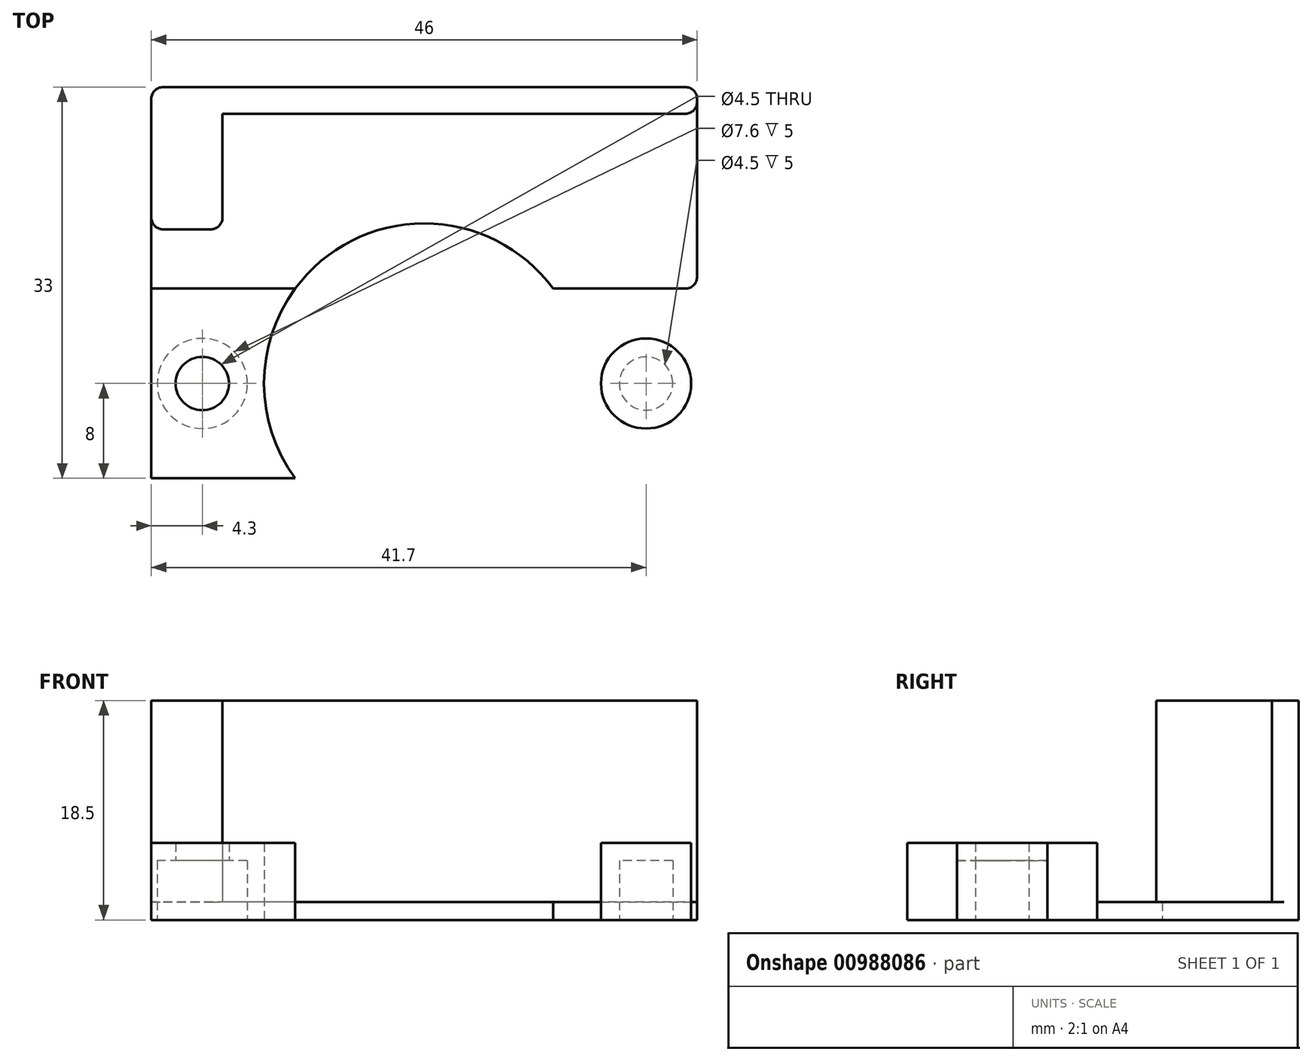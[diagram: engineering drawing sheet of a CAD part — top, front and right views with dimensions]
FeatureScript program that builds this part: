
annotation { "Feature Type Name" : "Feature", "Feature Type Description" : "" }
export const myFeature = defineFeature(function(context is Context, id is Id, definition is map)
    precondition{}
    {
        {
            var Q0;
            Q0=qCreatedBy(makeId("Top.planeOp"),FACE);
            var sketch = newSketch(context, id + "F0", { "sketchPlane" : qUnion([Q0])});
            skLineSegment(sketch, "E0.bottom", {"start": v(-23, 16.5) * mm, "end": v(23, 16.5) * mm});
            skLineSegment(sketch, "E0.top", {"start": v(-23, -16.5) * mm, "end": v(23, -16.5) * mm});
            skLineSegment(sketch, "E0.left", {"start": v(-23, 16.5) * mm, "end": v(-23, -16.5) * mm});
            skLineSegment(sketch, "E0.right", {"start": v(23, 16.5) * mm, "end": v(23, -16.5) * mm});
            skPoint(sketch, "E0.middle", {"position": v(0, 0) * mm});
            skPoint(sketch, "E1", {"position": v(0, -16.5) * mm});
            skCircle(sketch, "E2", {"center": v(-18.7, -8.5) * mm, "radius": 2.25 * mm});
            skLineSegment(sketch, "E3", {"start": v(0, 16.5) * mm, "end": v(0, -16.5) * mm, "construction": true});
            skCircle(sketch, "E4.MirrorC", {"center": v(18.7, -8.5) * mm, "radius": 2.25 * mm});
            skLineSegment(sketch, "E5", {"start": v(18.7, -8.5) * mm, "end": v(-18.7, -8.5) * mm, "construction": true});
            skCircle(sketch, "E6", {"center": v(0, -8.5) * mm, "radius": 13.5 * mm});
            skCircle(sketch, "E7", {"center": v(-18.7, -8.5) * mm, "radius": 3.8 * mm});
            skCircle(sketch, "E8.MirrorC", {"center": v(18.7, -8.5) * mm, "radius": 3.8 * mm});
            skLineSegment(sketch, "E9.bottom", {"start": v(-23, -0.5) * mm, "end": v(23, -0.5) * mm});
            skLineSegment(sketch, "E9.left", {"start": v(-23, -0.5) * mm, "end": v(-23, -16.5) * mm});
            skLineSegment(sketch, "E9.right", {"start": v(23, -0.5) * mm, "end": v(23, -16.5) * mm});
            skSolve(sketch);
        }
        {
            var Q0;
            Q0=makeQuery(id+"F0.imprint","IMPRINT",FACE,{"disambiguationData":[TD([[makeQuery(id+"F0.imprint","IMPRINT",EDGE,{"derivedFrom":sQuery(id+"F0.wireOp",EDGE,"E7")}),-1.0]])]});
            var Q1;
            Q1=makeQuery(id+"F0.imprint","IMPRINT",FACE,{"disambiguationData":[TD([[makeQuery(id+"F0.imprint","IMPRINT",EDGE,{"derivedFrom":sQuery(id+"F0.wireOp",EDGE,"E0.bottom")}),-1.0]])]});
            var Q2;
            Q2=makeQuery(id+"F0.imprint","IMPRINT",FACE,{"disambiguationData":[TD([[makeQuery(id+"F0.imprint","IMPRINT",EDGE,{"derivedFrom":sQuery(id+"F0.wireOp",EDGE,"E8.MirrorC")}),1.0]])]});
            extrude(context, id + "F1", {"entities" : qUnion([Q0, Q1, Q2]), "depth" : 1.5 * mm, "offsetDistance" : 25 * mm});
        }
        {
            var Q0;
            Q0=makeQuery(id+"F1.opExtrude","CAP_FACE",FACE,{"disambiguationData":[OSD([sQuery(id+"F0.wireOp",EDGE,"E0.bottom"),sQuery(id+"F0.wireOp",EDGE,"E0.top"),sQuery(id+"F0.wireOp",EDGE,"E0.left"),sQuery(id+"F0.wireOp",EDGE,"E0.right"),sQuery(id+"F0.wireOp",EDGE,"xRUmQ0dG-i3N2-o9Ad-kzeh-Mr6nwe9xlCmq.top"),sQuery(id+"F0.wireOp",EDGE,"xRUmQ0dG-i3N2-o9Ad-kzeh-Mr6nwe9xlCmq.left"),sQuery(id+"F0.wireOp",EDGE,"xRUmQ0dG-i3N2-o9Ad-kzeh-Mr6nwe9xlCmq.right"),sQuery(id+"F0.wireOp",EDGE,"E2"),sQuery(id+"F0.wireOp",EDGE,"E4.MirrorC")])],"isStart":false});
            var sketch = newSketch(context, id + "F2", { "sketchPlane" : qUnion([Q0])});
            skLineSegment(sketch, "E10.bottom", {"start": v(-23, 16.5) * mm, "end": v(23, 16.5) * mm});
            skLineSegment(sketch, "E10.top", {"start": v(-23, 4.5) * mm, "end": v(23, 4.5) * mm});
            skLineSegment(sketch, "E10.left", {"start": v(-23, 16.5) * mm, "end": v(-23, 4.5) * mm});
            skLineSegment(sketch, "E10.right", {"start": v(23, 16.5) * mm, "end": v(23, 4.5) * mm});
            skLineSegment(sketch, "E11.bottom", {"start": v(23, 6.75) * mm, "end": v(-17, 6.75) * mm});
            skLineSegment(sketch, "E11.top", {"start": v(23, 14.25) * mm, "end": v(-17, 14.25) * mm});
            skLineSegment(sketch, "E11.left", {"start": v(23, 14.25) * mm, "end": v(23, 6.75) * mm});
            skLineSegment(sketch, "E11.right", {"start": v(-17, 14.25) * mm, "end": v(-17, 6.75) * mm});
            skPoint(sketch, "E12", {"position": v(23, 10.5) * mm});
            skLineSegment(sketch, "E13.bottom", {"start": v(14, 6.75) * mm, "end": v(23, 6.75) * mm});
            skLineSegment(sketch, "E13.top", {"start": v(14, 4.5) * mm, "end": v(23, 4.5) * mm});
            skLineSegment(sketch, "E13.left", {"start": v(14, 6.75) * mm, "end": v(14, 4.5) * mm});
            skLineSegment(sketch, "E13.right", {"start": v(23, 6.75) * mm, "end": v(23, 4.5) * mm});
            skLineSegment(sketch, "E14.bottom", {"start": v(-17, 6.75) * mm, "end": v(-12, 6.75) * mm});
            skLineSegment(sketch, "E14.left", {"start": v(-17, 6.75) * mm, "end": v(-17, 4.5) * mm});
            skLineSegment(sketch, "E15", {"start": v(-12, 6.75) * mm, "end": v(-12, 4.5) * mm});
            skSolve(sketch);
        }
        {
            var Q0;
            Q0=makeQuery(id+"F2.imprint","IMPRINT",FACE,{"disambiguationData":[TD([[makeQuery(id+"F2.imprint","IMPRINT",EDGE,{"derivedFrom":sQuery(id+"F2.wireOp",EDGE,"E10.bottom")}),-1.0]])]});
            var Q1;
            Q1=makeQuery(id+"F2.imprint","IMPRINT",FACE,{"disambiguationData":[TD([[makeQuery(id+"F2.imprint","IMPRINT",EDGE,{"derivedFrom":sQuery(id+"F2.wireOp",EDGE,"E14.bottom")}),-1.0]])]});
            var Q2;
            Q2=makeQuery(id+"F2.imprint","IMPRINT",FACE,{"disambiguationData":[TD([[makeQuery(id+"F2.imprint","IMPRINT",EDGE,{"derivedFrom":sQuery(id+"F2.wireOp",EDGE,"E13.bottom")}),-1.0]])]});
            extrude(context, id + "F3", {"entities" : qUnion([Q0, Q1, Q2]), "operationType" : NewBodyOperationType.ADD, "depth" : 17 * mm, "offsetDistance" : 25 * mm});
        }
        {
            var Q0;
            Q0=makeQuery(id+"F3.boolean.opBoolean","MERGE",EDGE,{"derivedFrom":[makeQuery(id+"F1.opExtrude","SWEPT_EDGE",EDGE,{"disambiguationData":[OSD([sQuery(id+"F0.wireOp",EDGE,"E0.bottom"),sQuery(id+"F0.wireOp",EDGE,"E0.left")])]}),makeQuery(id+"F3.opExtrude","SWEPT_EDGE",EDGE,{"disambiguationData":[OSD([sQuery(id+"F2.wireOp",EDGE,"E10.bottom"),sQuery(id+"F2.wireOp",EDGE,"E10.left")])]})]});
            var Q1;
            Q1=makeQuery(id+"F3.boolean.opBoolean","MERGE",EDGE,{"derivedFrom":[makeQuery(id+"F1.opExtrude","SWEPT_EDGE",EDGE,{"disambiguationData":[OSD([sQuery(id+"F0.wireOp",EDGE,"E0.bottom"),sQuery(id+"F0.wireOp",EDGE,"E0.right")])]}),makeQuery(id+"F3.opExtrude","SWEPT_EDGE",EDGE,{"disambiguationData":[OSD([sQuery(id+"F2.wireOp",EDGE,"E10.bottom"),sQuery(id+"F2.wireOp",EDGE,"E10.right")])]})]});
            var Q2;
            Q2=makeQuery(id+"F3.opExtrude","SWEPT_EDGE",EDGE,{"disambiguationData":[OSD([sQuery(id+"F2.wireOp",EDGE,"E10.right"),sQuery(id+"F2.wireOp",EDGE,"E11.top"),sQuery(id+"F2.wireOp",EDGE,"E11.left")])]});
            var Q3;
            Q3=makeQuery(id+"F3.opExtrude","SWEPT_EDGE",EDGE,{"disambiguationData":[OSD([sQuery(id+"F2.wireOp",EDGE,"E11.left"),sQuery(id+"F2.wireOp",EDGE,"E13.bottom"),sQuery(id+"F2.wireOp",EDGE,"E13.right")])]});
            var Q4;
            Q4=makeQuery(id+"F3.opExtrude","SWEPT_EDGE",EDGE,{"disambiguationData":[OSD([sQuery(id+"F0.wireOp",EDGE,"E0.right"),sQuery(id+"F2.wireOp",EDGE,"E13.top"),sQuery(id+"F2.wireOp",EDGE,"E13.right")])]});
            var Q5;
            Q5=makeQuery(id+"F3.opExtrude","SWEPT_EDGE",EDGE,{"disambiguationData":[OSD([sQuery(id+"F2.wireOp",EDGE,"E11.bottom"),sQuery(id+"F2.wireOp",EDGE,"E14.bottom"),sQuery(id+"F2.wireOp",EDGE,"E14.right")])]});
            var Q6;
            Q6=makeQuery(id+"F3.opExtrude","SWEPT_EDGE",EDGE,{"disambiguationData":[OSD([sQuery(id+"F2.wireOp",EDGE,"E10.top"),sQuery(id+"F2.wireOp",EDGE,"E14.top"),sQuery(id+"F2.wireOp",EDGE,"E14.right")])]});
            var Q7;
            Q7=makeQuery(id+"F1.opExtrude","SWEPT_EDGE",EDGE,{"disambiguationData":[OSD([sQuery(id+"F0.wireOp",EDGE,"E0.top"),sQuery(id+"F0.wireOp",EDGE,"xRUmQ0dG-i3N2-o9Ad-kzeh-Mr6nwe9xlCmq.bottom"),sQuery(id+"F0.wireOp",EDGE,"xRUmQ0dG-i3N2-o9Ad-kzeh-Mr6nwe9xlCmq.left")])]});
            var Q8;
            Q8=makeQuery(id+"F1.opExtrude","SWEPT_EDGE",EDGE,{"disambiguationData":[OSD([sQuery(id+"F0.wireOp",EDGE,"E0.top"),sQuery(id+"F0.wireOp",EDGE,"E0.right")])]});
            var Q9;
            Q9=makeQuery(id+"F1.opExtrude","SWEPT_EDGE",EDGE,{"disambiguationData":[OSD([sQuery(id+"F0.wireOp",EDGE,"E0.top"),sQuery(id+"F0.wireOp",EDGE,"xRUmQ0dG-i3N2-o9Ad-kzeh-Mr6nwe9xlCmq.bottom"),sQuery(id+"F0.wireOp",EDGE,"xRUmQ0dG-i3N2-o9Ad-kzeh-Mr6nwe9xlCmq.right")])]});
            var Q10;
            Q10=makeQuery(id+"F1.opExtrude","SWEPT_EDGE",EDGE,{"disambiguationData":[OSD([sQuery(id+"F0.wireOp",EDGE,"E0.top"),sQuery(id+"F0.wireOp",EDGE,"E0.left")])]});
            var Q11;
            Q11=makeQuery(id+"F3.opExtrude","SWEPT_EDGE",EDGE,{"disambiguationData":[OSD([sQuery(id+"F0.wireOp",EDGE,"E0.left"),sQuery(id+"F2.wireOp",EDGE,"E10.top"),sQuery(id+"F2.wireOp",EDGE,"E10.left")])]});
            var Q12;
            Q12=makeQuery(id+"F3.opExtrude","SWEPT_EDGE",EDGE,{"disambiguationData":[OSD([sQuery(id+"F2.wireOp",EDGE,"E10.top"),sQuery(id+"F2.wireOp",EDGE,"E13.top"),sQuery(id+"F2.wireOp",EDGE,"E13.left")])]});
            var Q13;
            Q13=makeQuery(id+"F3.opExtrude","SWEPT_EDGE",EDGE,{"disambiguationData":[OSD([sQuery(id+"F2.wireOp",EDGE,"E11.bottom"),sQuery(id+"F2.wireOp",EDGE,"E13.bottom"),sQuery(id+"F2.wireOp",EDGE,"E13.left")])]});
            fillet(context, id + "F4", {"entities" : qUnion([Q0, Q1, Q2, Q3, Q4, Q5, Q6, Q7, Q8, Q9, Q10, Q11, Q12, Q13]), "radius" : 1 * mm, "tangentPropagation" : true, "allowEdgeOverflow" : false});
        }
        {
            var Q0;
            Q0=makeQuery(id+"F0.imprint","IMPRINT",FACE,{"disambiguationData":[TD([[makeQuery(id+"F0.imprint","IMPRINT",EDGE,{"derivedFrom":sQuery(id+"F0.wireOp",EDGE,"E7")}),-1.0]])]});
            var Q1;
            Q1=makeQuery(id+"F0.imprint","IMPRINT",FACE,{"disambiguationData":[TD([[makeQuery(id+"F0.imprint","IMPRINT",EDGE,{"derivedFrom":sQuery(id+"F0.wireOp",EDGE,"E8.MirrorC")}),1.0]])]});
            var Q2;
            Q2=makeQuery(id+"F0.imprint","IMPRINT",FACE,{"disambiguationData":[TD([[makeQuery(id+"F0.imprint","IMPRINT",EDGE,{"derivedFrom":sQuery(id+"F0.wireOp",EDGE,"E2")}),-1.0]])]});
            var Q3;
            Q3=makeQuery(id+"F0.imprint","IMPRINT",FACE,{"disambiguationData":[TD([[makeQuery(id+"F0.imprint","IMPRINT",EDGE,{"derivedFrom":sQuery(id+"F0.wireOp",EDGE,"E4.MirrorC")}),1.0]])]});
            extrude(context, id + "F5", {"entities" : qUnion([Q0, Q1, Q2, Q3]), "operationType" : NewBodyOperationType.ADD, "depth" : 6.5 * mm, "offsetDistance" : 25 * mm});
        }
        {
            var Q0;
            Q0=makeQuery(id+"F0.imprint","IMPRINT",FACE,{"disambiguationData":[TD([[makeQuery(id+"F0.imprint","IMPRINT",EDGE,{"derivedFrom":sQuery(id+"F0.wireOp",EDGE,"E2")}),-1.0]])]});
            var Q1;
            Q1=makeQuery(id+"F0.imprint","IMPRINT",FACE,{"disambiguationData":[TD([[makeQuery(id+"F0.imprint","IMPRINT",EDGE,{"derivedFrom":sQuery(id+"F0.wireOp",EDGE,"E4.MirrorC")}),1.0]])]});
            extrude(context, id + "F6", {"entities" : qUnion([Q0, Q1]), "operationType" : NewBodyOperationType.REMOVE, "depth" : 5 * mm, "offsetDistance" : 25 * mm});
        }
    });
